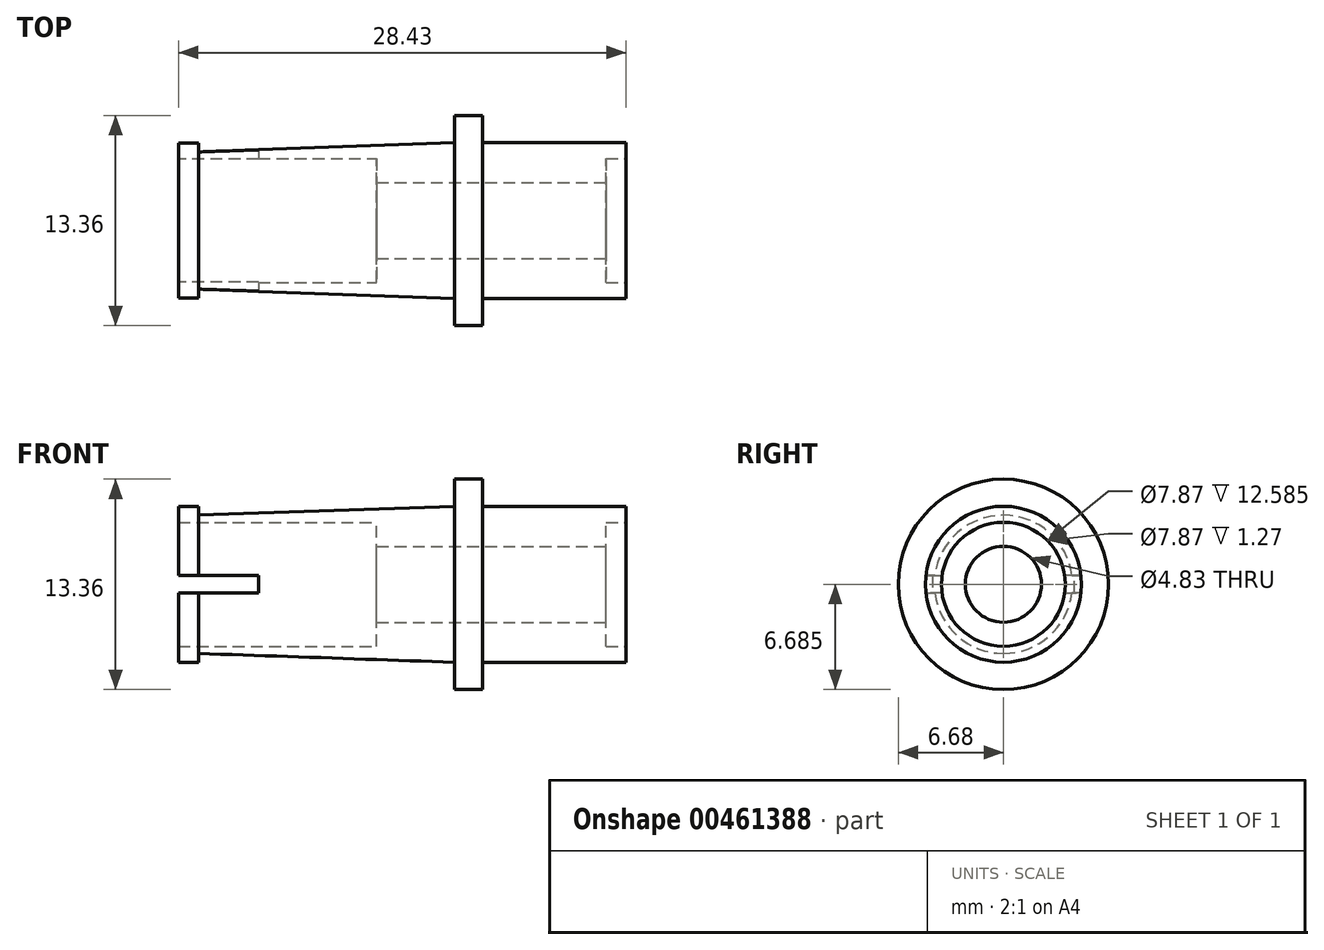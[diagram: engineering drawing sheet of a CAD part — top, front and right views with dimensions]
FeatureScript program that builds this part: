
annotation { "Feature Type Name" : "Feature", "Feature Type Description" : "" }
export const myFeature = defineFeature(function(context is Context, id is Id, definition is map)
    precondition{}
    {
        {
            var Q0;
            Q0=qCreatedBy(makeId("Front.planeOp"),FACE);
            var sketch = newSketch(context, id + "F0", { "sketchPlane" : qUnion([Q0])});
            skLineSegment(sketch, "E0", {"start": v(1.26, -9.09) * mm, "end": v(9.64, -9.09) * mm});
            skLineSegment(sketch, "E1", {"start": v(9.64, -9.09) * mm, "end": v(9.64, -10.61) * mm});
            skLineSegment(sketch, "E2", {"start": v(9.64, -10.61) * mm, "end": v(10.9, -10.61) * mm});
            skLineSegment(sketch, "E3", {"start": v(10.9, -10.61) * mm, "end": v(10.9, -11.63) * mm});
            skLineSegment(sketch, "E4", {"start": v(10.9, -11.63) * mm, "end": v(1.78, -11.63) * mm});
            skLineSegment(sketch, "E5", {"start": v(1.78, -11.63) * mm, "end": v(1.78, -13.36) * mm});
            skLineSegment(sketch, "E6", {"start": v(1.78, -13.36) * mm, "end": v(0, -13.36) * mm});
            skLineSegment(sketch, "E7", {"start": v(0, -13.36) * mm, "end": v(0, -11.63) * mm});
            skLineSegment(sketch, "E8", {"start": v(0, -11.63) * mm, "end": v(-16.25, -11.07) * mm});
            skLineSegment(sketch, "E9", {"start": v(-16.25, -11.07) * mm, "end": v(-16.25, -11.63) * mm});
            skLineSegment(sketch, "E10", {"start": v(-16.25, -11.63) * mm, "end": v(-17.52, -11.63) * mm});
            skLineSegment(sketch, "E11", {"start": v(-17.52, -11.63) * mm, "end": v(-17.52, -10.61) * mm});
            skLineSegment(sketch, "E12", {"start": v(-17.52, -10.61) * mm, "end": v(-16.25, -10.61) * mm});
            skLineSegment(sketch, "E13", {"start": v(-16.25, -10.61) * mm, "end": v(-4.94, -10.61) * mm});
            skLineSegment(sketch, "E14", {"start": v(-4.94, -10.61) * mm, "end": v(-4.94, -9.09) * mm});
            skLineSegment(sketch, "E15", {"start": v(1.26, -9.09) * mm, "end": v(1.26, -6.68) * mm});
            skLineSegment(sketch, "E16", {"start": v(-4.94, -9.09) * mm, "end": v(0, -9.09) * mm});
            skLineSegment(sketch, "E17", {"start": v(0, -9.09) * mm, "end": v(0, -6.68) * mm});
            skLineSegment(sketch, "E18.MirrorCS", {"start": v(-16.25, -2.28) * mm, "end": v(-16.25, -1.72) * mm});
            skLineSegment(sketch, "E19.MirrorCS", {"start": v(-17.52, -1.72) * mm, "end": v(-17.52, -2.74) * mm});
            skLineSegment(sketch, "E20.MirrorCS", {"start": v(-16.25, -1.72) * mm, "end": v(-17.52, -1.72) * mm});
            skLineSegment(sketch, "E21.MirrorCS", {"start": v(-17.52, -2.74) * mm, "end": v(-16.25, -2.74) * mm});
            skLineSegment(sketch, "E22.MirrorCS", {"start": v(10.9, -2.74) * mm, "end": v(10.9, -1.72) * mm});
            skLineSegment(sketch, "E23.MirrorCS", {"start": v(9.64, -2.74) * mm, "end": v(10.9, -2.74) * mm});
            skLineSegment(sketch, "E24.MirrorCS", {"start": v(0, -4.26) * mm, "end": v(0, -6.68) * mm});
            skLineSegment(sketch, "E25.MirrorCS", {"start": v(1.26, -4.26) * mm, "end": v(1.26, -6.68) * mm});
            skLineSegment(sketch, "E26.MirrorCS", {"start": v(-4.94, -4.26) * mm, "end": v(0, -4.26) * mm});
            skLineSegment(sketch, "E27.MirrorCS", {"start": v(1.78, 0) * mm, "end": v(0, 0) * mm});
            skLineSegment(sketch, "E28.MirrorCS", {"start": v(0, -1.72) * mm, "end": v(-16.25, -2.28) * mm});
            skLineSegment(sketch, "E29.MirrorCS", {"start": v(-4.94, -2.74) * mm, "end": v(-4.94, -4.26) * mm});
            skLineSegment(sketch, "E30.MirrorCS", {"start": v(0, 0) * mm, "end": v(0, -1.72) * mm});
            skLineSegment(sketch, "E31.MirrorCS", {"start": v(10.9, -1.72) * mm, "end": v(1.78, -1.72) * mm});
            skLineSegment(sketch, "E32.MirrorCS", {"start": v(-16.25, -2.74) * mm, "end": v(-4.94, -2.74) * mm});
            skLineSegment(sketch, "E33.MirrorCS", {"start": v(9.64, -4.26) * mm, "end": v(9.64, -2.74) * mm});
            skLineSegment(sketch, "E34.MirrorCS", {"start": v(1.78, -1.72) * mm, "end": v(1.78, 0) * mm});
            skLineSegment(sketch, "E35.MirrorCS", {"start": v(1.26, -4.26) * mm, "end": v(9.64, -4.26) * mm});
            skLineSegment(sketch, "E36", {"start": v(22.94, -6.68) * mm, "end": v(-37.53, -6.68) * mm, "construction": true});
            skLineSegment(sketch, "E37", {"start": v(9.64, -6.68) * mm, "end": v(-16.25, -6.68) * mm});
            skSolve(sketch);
        }
        {
            var Q0;
            Q0=makeQuery(id+"F0.imprint","IMPRINT",FACE,{"disambiguationData":[TD([[makeQuery(id+"F0.imprint","IMPRINT",EDGE,{"derivedFrom":sQuery(id+"F0.wireOp",EDGE,"E0")}),-1.0]])]});
            var Q1;
            Q1=sQuery(id+"F0.wireOp",EDGE,"E37");
            revolve(context, id + "F1", {"entities" : qUnion([Q0]), "axis" : qUnion([Q1]), "revolveType" : RevolveType.FULL});
        }
        {
            var Q0;
            Q0=makeQuery(id+"F1.opRevolve","SWEPT_FACE",FACE,{"disambiguationData":[OSD([sQuery(id+"F0.wireOp",EDGE,"E11")])]});
            var sketch = newSketch(context, id + "F2", { "sketchPlane" : qUnion([Q0])});
            skLineSegment(sketch, "E38", {"start": v(-4.92, -6.13) * mm, "end": v(-3.9, -6.13) * mm});
            skLineSegment(sketch, "E39", {"start": v(-3.9, -6.13) * mm, "end": v(-3.9, -7.22) * mm});
            skLineSegment(sketch, "E40", {"start": v(-3.9, -7.22) * mm, "end": v(-4.92, -7.22) * mm});
            skLineSegment(sketch, "E41.MirrorCS", {"start": v(3.9, -7.22) * mm, "end": v(4.92, -7.22) * mm});
            skLineSegment(sketch, "E42.MirrorCS", {"start": v(4.92, -6.13) * mm, "end": v(3.9, -6.13) * mm});
            skSolve(sketch);
        }
        {
            var Q0;
            {var subQ0=sQuery(id+"F2.wireOp",EDGE,"E38");Q0=makeQuery(id+"F2.imprint","IMPRINT",FACE,{"disambiguationData":[TD([[makeQuery(id+"F2.imprint","IMPRINT",EDGE,{"derivedFrom":subQ0}),-1.0]])]});}
            var Q1;
            {var subQ0=sQuery(id+"F2.wireOp",EDGE,"E41.MirrorCS");Q1=makeQuery(id+"F2.imprint","IMPRINT",FACE,{"disambiguationData":[TD([[makeQuery(id+"F2.imprint","IMPRINT",EDGE,{"derivedFrom":subQ0}),1.0]])]});}
            extrude(context, id + "F3", {"entities" : qUnion([Q0, Q1]), "operationType" : NewBodyOperationType.REMOVE, "oppositeDirection" : true, "depth" : 5.08 * mm});
        }
        {
            var Q0;
            Q0=makeQuery(id+"F1.opRevolve","SWEPT_FACE",FACE,{"disambiguationData":[OSD([sQuery(id+"F0.wireOp",EDGE,"E15")])]});
            extrude(context, id + "F4", {"entities" : qUnion([Q0]), "operationType" : NewBodyOperationType.REMOVE, "oppositeDirection" : true, "depth" : 25.4 * mm});
        }
    });
